# Revit family: Curtainwall_T2500_Transom-Door-With-Double-Sidelites_Cross-Aluminum
name_source: partatom
category: Generic Models
units: mm (PartAtom-declared; Revit-internal decimal feet)

## family parameters
Always vertical = Yes
Can host rebar = No
Cut with Voids When Loaded = No
Host = Wall
Maintain Annotation Orientation = No
Part Type = Normal
Room Calculation Point = No
Round Connector Dimension = Use Diameter
Shared = No

## types (1)
- T2500_Transom-Door-Frame-With-Double-Sidelites
    Default Elevation = 0' - 0"
    Door Height = 6' - 8"
    Door Width = 4' - 0"
    Frame Material = Frame
    Glazing Material = Glass
    Keynote = 08 44 00
    Manufacturer = Cross Aluminum
    Model = T2500_Transom-Door-Frame-With-Double-Sidelites
    Offset From Hori. Mid-Rails Height = 3' - 0"
    Product Page URL = https://www.crossaluminum.com
    Total Height = 10' - 0"
    Total Width = 13' - 0"
    URL = https://www.crossaluminum.com

## geometry (parser evidence)
native form markers: Sweep x3
no freeform markers — native parametric forms only
